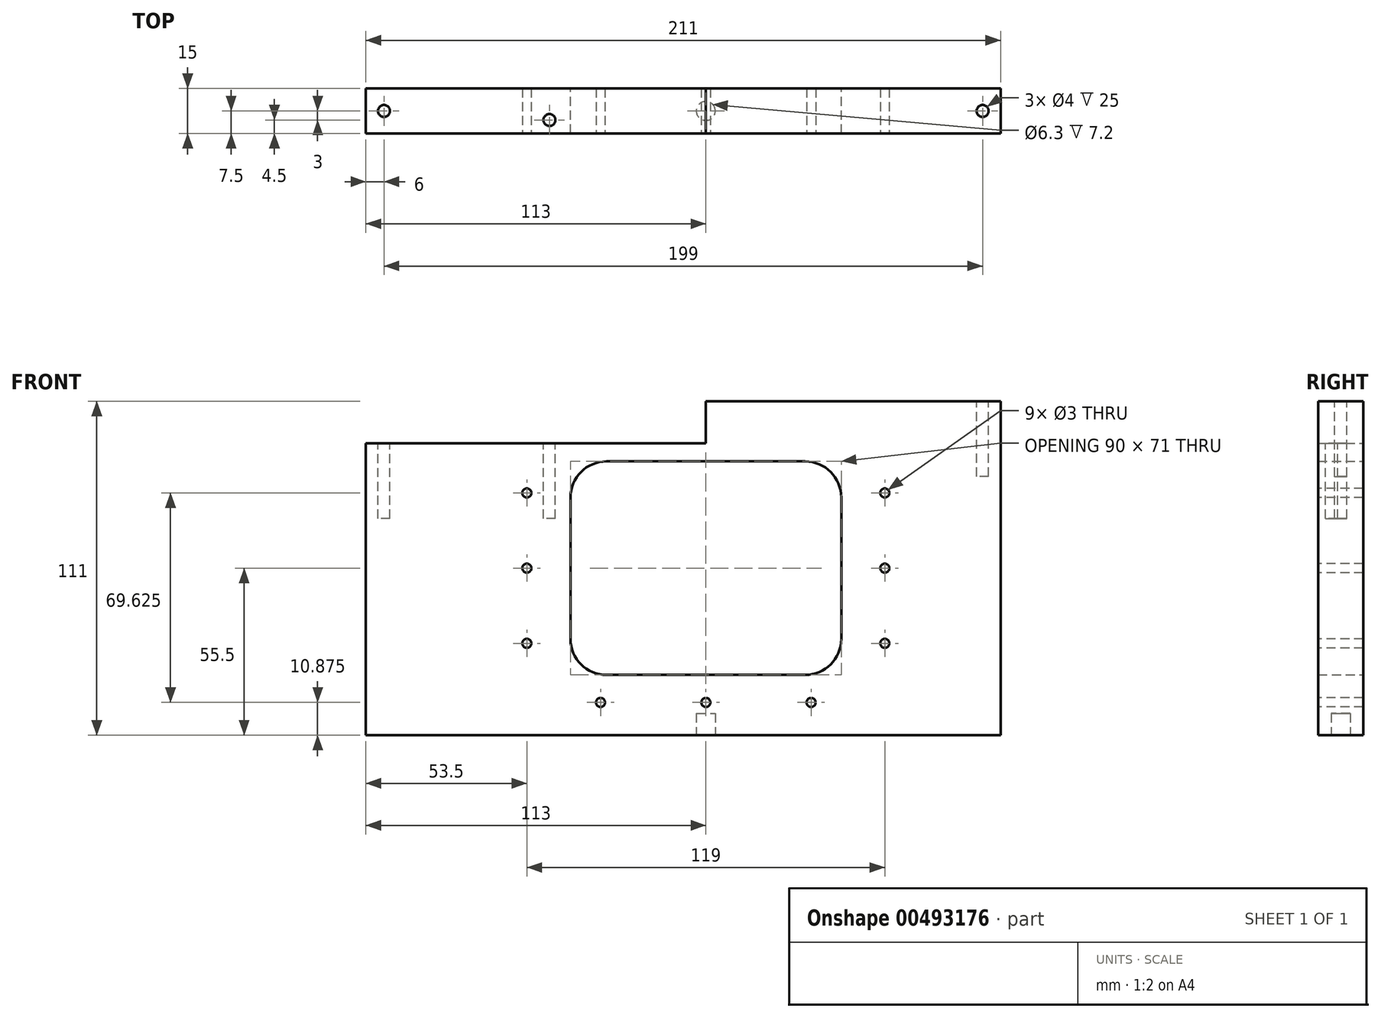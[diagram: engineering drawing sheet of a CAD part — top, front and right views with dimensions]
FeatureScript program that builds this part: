
annotation { "Feature Type Name" : "Feature", "Feature Type Description" : "" }
export const myFeature = defineFeature(function(context is Context, id is Id, definition is map)
    precondition{}
    {
        {
            var Q0;
            Q0=qCreatedBy(makeId("Front.planeOp"),FACE);
            var sketch = newSketch(context, id + "F0", { "sketchPlane" : qUnion([Q0])});
            skLineSegment(sketch, "E0.bottom", {"start": v(113, 55.5) * mm, "end": v(-113, 55.5) * mm});
            skLineSegment(sketch, "E0.top", {"start": v(113, -55.5) * mm, "end": v(-113, -55.5) * mm});
            skLineSegment(sketch, "E0.left", {"start": v(113, 55.5) * mm, "end": v(113, -55.5) * mm});
            skLineSegment(sketch, "E0.right", {"start": v(-113, 55.5) * mm, "end": v(-113, -55.5) * mm});
            skPoint(sketch, "E0.middle", {"position": v(0, 0) * mm});
            skLineSegment(sketch, "E1.bottom", {"start": v(45, 35.5) * mm, "end": v(-45, 35.5) * mm});
            skLineSegment(sketch, "E1.top", {"start": v(45, -35.5) * mm, "end": v(-45, -35.5) * mm});
            skLineSegment(sketch, "E1.left", {"start": v(45, 35.5) * mm, "end": v(45, -35.5) * mm});
            skLineSegment(sketch, "E1.right", {"start": v(-45, 35.5) * mm, "end": v(-45, -35.5) * mm});
            skSolve(sketch);
        }
        {
            var Q0;
            Q0=qSketchRegion(id+"F0",true);
            extrude(context, id + "F1", {"entities" : qUnion([Q0]), "depth" : 15 * mm});
        }
        {
            var Q0;
            Q0=makeQuery(id+"F1.opExtrude","SWEPT_EDGE",EDGE,{"disambiguationData":[OSD([sQuery(id+"F0.wireOp",EDGE,"E1.bottom"),sQuery(id+"F0.wireOp",EDGE,"E1.left")])]});
            var Q1;
            Q1=makeQuery(id+"F1.opExtrude","SWEPT_EDGE",EDGE,{"disambiguationData":[OSD([sQuery(id+"F0.wireOp",EDGE,"E1.top"),sQuery(id+"F0.wireOp",EDGE,"E1.left")])]});
            var Q2;
            Q2=makeQuery(id+"F1.opExtrude","SWEPT_EDGE",EDGE,{"disambiguationData":[OSD([sQuery(id+"F0.wireOp",EDGE,"E1.top"),sQuery(id+"F0.wireOp",EDGE,"E1.right")])]});
            var Q3;
            Q3=makeQuery(id+"F1.opExtrude","SWEPT_EDGE",EDGE,{"disambiguationData":[OSD([sQuery(id+"F0.wireOp",EDGE,"E1.bottom"),sQuery(id+"F0.wireOp",EDGE,"E1.right")])]});
            fillet(context, id + "F2", {"entities" : qUnion([Q0, Q1, Q2, Q3]), "radius" : 12 * mm, "tangentPropagation" : true, "allowEdgeOverflow" : false});
        }
        {
            var Q0;
            Q0=makeQuery(id+"F1.opExtrude","CAP_FACE",FACE,{"disambiguationData":[OSD([sQuery(id+"F0.wireOp",EDGE,"E0.bottom"),sQuery(id+"F0.wireOp",EDGE,"E0.top"),sQuery(id+"F0.wireOp",EDGE,"E0.left"),sQuery(id+"F0.wireOp",EDGE,"E0.right"),sQuery(id+"F0.wireOp",EDGE,"E1.bottom"),sQuery(id+"F0.wireOp",EDGE,"E1.top"),sQuery(id+"F0.wireOp",EDGE,"E1.left"),sQuery(id+"F0.wireOp",EDGE,"E1.right")])],"isStart":false});
            var sketch = newSketch(context, id + "F3", { "sketchPlane" : qUnion([Q0])});
            skLineSegment(sketch, "E2.bottom", {"start": v(59.5, 41.35) * mm, "end": v(-59.5, 41.35) * mm, "construction": true});
            skLineSegment(sketch, "E2.top", {"start": v(59.5, -41.35) * mm, "end": v(-59.5, -41.35) * mm, "construction": true});
            skLineSegment(sketch, "E2.left", {"start": v(59.5, 41.35) * mm, "end": v(59.5, -41.35) * mm, "construction": true});
            skLineSegment(sketch, "E2.right", {"start": v(-59.5, 41.35) * mm, "end": v(-59.5, -41.35) * mm, "construction": true});
            skPoint(sketch, "E2.middle", {"position": v(0, 0) * mm});
            skCircle(sketch, "E3", {"center": v(-59.5, 0) * mm, "radius": 1.5 * mm});
            skCircle(sketch, "E4", {"center": v(-59.5, 25) * mm, "radius": 1.5 * mm});
            skCircle(sketch, "E5", {"center": v(-59.5, -25) * mm, "radius": 1.5 * mm});
            skCircle(sketch, "E6", {"center": v(59.5, 0) * mm, "radius": 1.5 * mm});
            skCircle(sketch, "E7", {"center": v(59.5, 25) * mm, "radius": 1.5 * mm});
            skCircle(sketch, "E8", {"center": v(59.5, -25) * mm, "radius": 1.5 * mm});
            skSolve(sketch);
        }
        {
            var Q0;
            Q0 = qSketchRegion(id + "F3", true);
            extrude(context, id + "F4", {"entities" : qUnion([Q0]), "operationType" : NewBodyOperationType.REMOVE, "oppositeDirection" : true, "depth" : 25 * mm});
        }
        {
            var Q0;
            Q0=makeQuery(id+"F1.opExtrude","CAP_FACE",FACE,{"disambiguationData":[OSD([sQuery(id+"F0.wireOp",EDGE,"E0.bottom"),sQuery(id+"F0.wireOp",EDGE,"E0.top"),sQuery(id+"F0.wireOp",EDGE,"E0.left"),sQuery(id+"F0.wireOp",EDGE,"E0.right"),sQuery(id+"F0.wireOp",EDGE,"E1.bottom"),sQuery(id+"F0.wireOp",EDGE,"E1.top"),sQuery(id+"F0.wireOp",EDGE,"E1.left"),sQuery(id+"F0.wireOp",EDGE,"E1.right")])],"isStart":false});
            var sketch = newSketch(context, id + "F5", { "sketchPlane" : qUnion([Q0])});
            skLineSegment(sketch, "E9.bottom", {"start": v(47.67, 50.3) * mm, "end": v(-47.67, 50.3) * mm, "construction": true});
            skLineSegment(sketch, "E9.top", {"start": v(47.67, 44.63) * mm, "end": v(-47.67, 44.62) * mm, "construction": true});
            skLineSegment(sketch, "E9.left", {"start": v(47.67, 50.3) * mm, "end": v(47.67, 44.62) * mm, "construction": true});
            skLineSegment(sketch, "E9.right", {"start": v(-47.67, 50.3) * mm, "end": v(-47.67, 44.62) * mm, "construction": true});
            skPoint(sketch, "E9.middle", {"position": v(0, 47.46) * mm});
            skLineSegment(sketch, "E10.bottom", {"start": v(52.2, -44.62) * mm, "end": v(-52.2, -44.63) * mm, "construction": true});
            skLineSegment(sketch, "E10.top", {"start": v(52.2, -49.16) * mm, "end": v(-52.2, -49.16) * mm, "construction": true});
            skLineSegment(sketch, "E10.left", {"start": v(52.2, -44.62) * mm, "end": v(52.2, -49.16) * mm, "construction": true});
            skLineSegment(sketch, "E10.right", {"start": v(-52.2, -44.63) * mm, "end": v(-52.2, -49.16) * mm, "construction": true});
            skPoint(sketch, "E10.middle", {"position": v(0, -46.9) * mm});
            skCircle(sketch, "E11", {"center": v(0, -44.62) * mm, "radius": 1.5 * mm});
            skCircle(sketch, "E12", {"center": v(35, -44.62) * mm, "radius": 1.5 * mm});
            skCircle(sketch, "E13", {"center": v(0, 44.62) * mm, "radius": 1.5 * mm});
            skCircle(sketch, "E14", {"center": v(-35, 44.62) * mm, "radius": 1.5 * mm});
            skCircle(sketch, "E15", {"center": v(-35, -44.63) * mm, "radius": 1.5 * mm});
            skCircle(sketch, "E16", {"center": v(35, 44.63) * mm, "radius": 1.5 * mm});
            skSolve(sketch);
        }
        {
            var Q0;
            Q0 = qSketchRegion(id + "F5", true);
            extrude(context, id + "F6", {"entities" : qUnion([Q0]), "operationType" : NewBodyOperationType.REMOVE, "oppositeDirection" : true, "depth" : 25 * mm});
        }
        {
            var Q0;
            Q0=makeQuery(id+"F1.opExtrude","SWEPT_FACE",FACE,{"disambiguationData":[OSD([sQuery(id+"F0.wireOp",EDGE,"E0.bottom")])]});
            var sketch = newSketch(context, id + "F7", { "sketchPlane" : qUnion([Q0])});
            skLineSegment(sketch, "E17.bottom", {"start": v(113, 0) * mm, "end": v(88, 0) * mm});
            skLineSegment(sketch, "E17.top", {"start": v(113, -15) * mm, "end": v(88, -15) * mm});
            skLineSegment(sketch, "E17.left", {"start": v(113, 0) * mm, "end": v(113, -15) * mm});
            skLineSegment(sketch, "E17.right", {"start": v(88, 0) * mm, "end": v(88, -15) * mm});
            skSolve(sketch);
        }
        {
            var Q0;
            Q0 = qSketchRegion(id + "F7", true);
            extrude(context, id + "F8", {"entities" : qUnion([Q0]), "operationType" : NewBodyOperationType.REMOVE, "oppositeDirection" : true, "depth" : 115.3 * mm});
        }
        {
            var Q0;
            Q0=makeQuery(id+"F1.opExtrude","SWEPT_FACE",FACE,{"disambiguationData":[OSD([sQuery(id+"F0.wireOp",EDGE,"E0.bottom")])]});
            var sketch = newSketch(context, id + "F9", { "sketchPlane" : qUnion([Q0])});
            skLineSegment(sketch, "E18.bottom", {"start": v(88, 0) * mm, "end": v(-113, 0) * mm});
            skLineSegment(sketch, "E18.top", {"start": v(88, -15) * mm, "end": v(-113, -15) * mm});
            skLineSegment(sketch, "E18.left", {"start": v(88, 0) * mm, "end": v(88, -15) * mm});
            skLineSegment(sketch, "E18.right", {"start": v(-113, 0) * mm, "end": v(-113, -15) * mm});
            skSolve(sketch);
        }
        {
            var Q0;
            Q0 = qSketchRegion(id + "F9", true);
            extrude(context, id + "F10", {"entities" : qUnion([Q0]), "operationType" : NewBodyOperationType.REMOVE, "oppositeDirection" : true, "depth" : 14 * mm});
        }
        {
            var Q0;
            Q0=makeQuery(id+"F10.boolean.opBoolean","COPY",FACE,{"derivedFrom":makeQuery(id+"F10.opExtrude","CAP_FACE",FACE,{"disambiguationData":[OSD([sQuery(id+"F9.wireOp",EDGE,"E18.bottom"),sQuery(id+"F9.wireOp",EDGE,"E18.top"),sQuery(id+"F9.wireOp",EDGE,"E18.left"),sQuery(id+"F9.wireOp",EDGE,"E18.right")])],"isStart":false})});
            var sketch = newSketch(context, id + "F11", { "sketchPlane" : qUnion([Q0])});
            skLineSegment(sketch, "E19.bottom", {"start": v(88, 0) * mm, "end": v(0, 0) * mm});
            skLineSegment(sketch, "E19.top", {"start": v(88, -15) * mm, "end": v(0, -15) * mm});
            skLineSegment(sketch, "E19.left", {"start": v(88, 0) * mm, "end": v(88, -15) * mm});
            skLineSegment(sketch, "E19.right", {"start": v(0, 0) * mm, "end": v(0, -15) * mm});
            skSolve(sketch);
        }
        {
            var Q0;
            Q0 = qSketchRegion(id + "F11", true);
            extrude(context, id + "F12", {"entities" : qUnion([Q0]), "operationType" : NewBodyOperationType.ADD, "depth" : 14 * mm});
        }
        {
            var Q0;
            Q0=makeQuery(id+"F12.opExtrude","CAP_FACE",FACE,{"disambiguationData":[OSD([sQuery(id+"F11.wireOp",EDGE,"E19.bottom"),sQuery(id+"F11.wireOp",EDGE,"E19.top"),sQuery(id+"F11.wireOp",EDGE,"E19.left"),sQuery(id+"F11.wireOp",EDGE,"E19.right")])],"isStart":false});
            var sketch = newSketch(context, id + "F13", { "sketchPlane" : qUnion([Q0])});
            skLineSegment(sketch, "E20.bottom", {"start": v(63, 0) * mm, "end": v(-18, 0) * mm});
            skLineSegment(sketch, "E20.top", {"start": v(63, -65) * mm, "end": v(-18, -65) * mm});
            skLineSegment(sketch, "E20.left", {"start": v(63, 0) * mm, "end": v(63, -65) * mm});
            skLineSegment(sketch, "E20.right", {"start": v(-18, 0) * mm, "end": v(-18, -65) * mm});
            skSolve(sketch);
        }
        {
            var Q0;
            Q0 = qSketchRegion(id + "F13", true);
            extrude(context, id + "F14", {"entities" : qUnion([Q0]), "operationType" : NewBodyOperationType.ADD, "depth" : 5 * mm});
        }
        {
            var Q0;
            Q0=makeQuery(id+"F12.opExtrude","CAP_FACE",FACE,{"disambiguationData":[OSD([sQuery(id+"F11.wireOp",EDGE,"E19.bottom"),sQuery(id+"F11.wireOp",EDGE,"E19.top"),sQuery(id+"F11.wireOp",EDGE,"E19.left"),sQuery(id+"F11.wireOp",EDGE,"E19.right")])],"isStart":false});
            var sketch = newSketch(context, id + "F15", { "sketchPlane" : qUnion([Q0])});
            skLineSegment(sketch, "E21.bottom", {"start": v(88, 0) * mm, "end": v(98, 0) * mm});
            skLineSegment(sketch, "E21.top", {"start": v(88, -15) * mm, "end": v(98, -15) * mm});
            skLineSegment(sketch, "E21.left", {"start": v(88, 0) * mm, "end": v(88, -15) * mm});
            skLineSegment(sketch, "E21.right", {"start": v(98, 0) * mm, "end": v(98, -15) * mm});
            skSolve(sketch);
        }
        {
            var Q0;
            Q0 = qSketchRegion(id + "F15", true);
            extrude(context, id + "F16", {"entities" : qUnion([Q0]), "operationType" : NewBodyOperationType.ADD, "oppositeDirection" : true, "depth" : 111 * mm});
        }
        {
            var Q0;
            Q0=makeQuery(id+"F14.opExtrude","CAP_FACE",FACE,{"disambiguationData":[OSD([sQuery(id+"F13.wireOp",EDGE,"E20.bottom"),sQuery(id+"F13.wireOp",EDGE,"E20.top"),sQuery(id+"F13.wireOp",EDGE,"E20.left"),sQuery(id+"F13.wireOp",EDGE,"E20.right")])],"isStart":false});
            var sketch = newSketch(context, id + "F17", { "sketchPlane" : qUnion([Q0])});
            skLineSegment(sketch, "E22.bottom", {"start": v(-18, 0) * mm, "end": v(63, 0) * mm});
            skLineSegment(sketch, "E22.top", {"start": v(-18, -65) * mm, "end": v(63, -65) * mm});
            skLineSegment(sketch, "E22.left", {"start": v(-18, 0) * mm, "end": v(-18, -65) * mm});
            skLineSegment(sketch, "E22.right", {"start": v(63, 0) * mm, "end": v(63, -65) * mm});
            skSolve(sketch);
        }
        {
            var Q0;
            Q0 = qSketchRegion(id + "F17", true);
            extrude(context, id + "F18", {"entities" : qUnion([Q0]), "operationType" : NewBodyOperationType.REMOVE, "oppositeDirection" : true, "depth" : 5 * mm});
        }
        {
            var Q0;
            Q0=makeQuery(id+"F10.boolean.opBoolean","COPY",FACE,{"derivedFrom":makeQuery(id+"F10.opExtrude","CAP_FACE",FACE,{"disambiguationData":[OSD([sQuery(id+"F9.wireOp",EDGE,"E18.bottom"),sQuery(id+"F9.wireOp",EDGE,"E18.top"),sQuery(id+"F9.wireOp",EDGE,"E18.left"),sQuery(id+"F9.wireOp",EDGE,"E18.right")])],"isStart":false})});
            var sketch = newSketch(context, id + "F19", { "sketchPlane" : qUnion([Q0])});
            skCircle(sketch, "E23", {"center": v(-52, -10.5) * mm, "radius": 2 * mm});
            skSolve(sketch);
        }
        {
            var Q0;
            Q0 = qSketchRegion(id + "F19", true);
            extrude(context, id + "F20", {"entities" : qUnion([Q0]), "operationType" : NewBodyOperationType.REMOVE, "oppositeDirection" : true, "depth" : 25 * mm});
        }
        {
            var Q0;
            Q0=makeQuery(id+"F16.boolean.opBoolean","MERGE",FACE,{"derivedFrom":[makeQuery(id+"F1.opExtrude","SWEPT_FACE",FACE,{"disambiguationData":[OSD([sQuery(id+"F0.wireOp",EDGE,"E0.top")])]}),makeQuery(id+"F16.opExtrude","CAP_FACE",FACE,{"disambiguationData":[OSD([sQuery(id+"F15.wireOp",EDGE,"E21.bottom"),sQuery(id+"F15.wireOp",EDGE,"E21.top"),sQuery(id+"F15.wireOp",EDGE,"E21.left"),sQuery(id+"F15.wireOp",EDGE,"E21.right")])],"isStart":false})]});
            var sketch = newSketch(context, id + "F21", { "sketchPlane" : qUnion([Q0])});
            skCircle(sketch, "E24", {"center": v(0, 7.5) * mm, "radius": 3.15 * mm});
            skSolve(sketch);
        }
        {
            var Q0;
            Q0 = qSketchRegion(id + "F21", true);
            extrude(context, id + "F22", {"entities" : qUnion([Q0]), "operationType" : NewBodyOperationType.REMOVE, "oppositeDirection" : true, "depth" : 7.2 * mm});
        }
        {
            var Q0;
            Q0=makeQuery(id+"F10.boolean.opBoolean","COPY",FACE,{"derivedFrom":makeQuery(id+"F10.opExtrude","CAP_FACE",FACE,{"disambiguationData":[OSD([sQuery(id+"F9.wireOp",EDGE,"E18.bottom"),sQuery(id+"F9.wireOp",EDGE,"E18.top"),sQuery(id+"F9.wireOp",EDGE,"E18.left"),sQuery(id+"F9.wireOp",EDGE,"E18.right")])],"isStart":false})});
            var sketch = newSketch(context, id + "F23", { "sketchPlane" : qUnion([Q0])});
            skCircle(sketch, "E25", {"center": v(-107, -7.5) * mm, "radius": 2 * mm});
            skSolve(sketch);
        }
        {
            var Q0;
            Q0 = qSketchRegion(id + "F23", true);
            extrude(context, id + "F24", {"entities" : qUnion([Q0]), "operationType" : NewBodyOperationType.REMOVE, "oppositeDirection" : true, "depth" : 25 * mm});
        }
        {
            var Q0;
            Q0=makeQuery(id+"F18.boolean.opBoolean","MERGE",FACE,{"derivedFrom":[makeQuery(id+"F16.boolean.opBoolean","MERGE",FACE,{"derivedFrom":[makeQuery(id+"F12.opExtrude","CAP_FACE",FACE,{"disambiguationData":[OSD([sQuery(id+"F11.wireOp",EDGE,"E19.bottom"),sQuery(id+"F11.wireOp",EDGE,"E19.top"),sQuery(id+"F11.wireOp",EDGE,"E19.left"),sQuery(id+"F11.wireOp",EDGE,"E19.right")])],"isStart":false}),makeQuery(id+"F16.opExtrude","CAP_FACE",FACE,{"disambiguationData":[OSD([sQuery(id+"F15.wireOp",EDGE,"E21.bottom"),sQuery(id+"F15.wireOp",EDGE,"E21.top"),sQuery(id+"F15.wireOp",EDGE,"E21.left"),sQuery(id+"F15.wireOp",EDGE,"E21.right")])],"isStart":true})]}),makeQuery(id+"F18.opExtrude","CAP_FACE",FACE,{"disambiguationData":[OSD([sQuery(id+"F17.wireOp",EDGE,"E22.bottom"),sQuery(id+"F17.wireOp",EDGE,"E22.top"),sQuery(id+"F17.wireOp",EDGE,"E22.left"),sQuery(id+"F17.wireOp",EDGE,"E22.right")])],"isStart":false})]});
            var sketch = newSketch(context, id + "F25", { "sketchPlane" : qUnion([Q0])});
            skCircle(sketch, "E26", {"center": v(92, -7.5) * mm, "radius": 2 * mm});
            skSolve(sketch);
        }
        {
            var Q0;
            Q0 = qSketchRegion(id + "F25", true);
            extrude(context, id + "F26", {"entities" : qUnion([Q0]), "operationType" : NewBodyOperationType.REMOVE, "oppositeDirection" : true, "depth" : 25 * mm});
        }
    });
